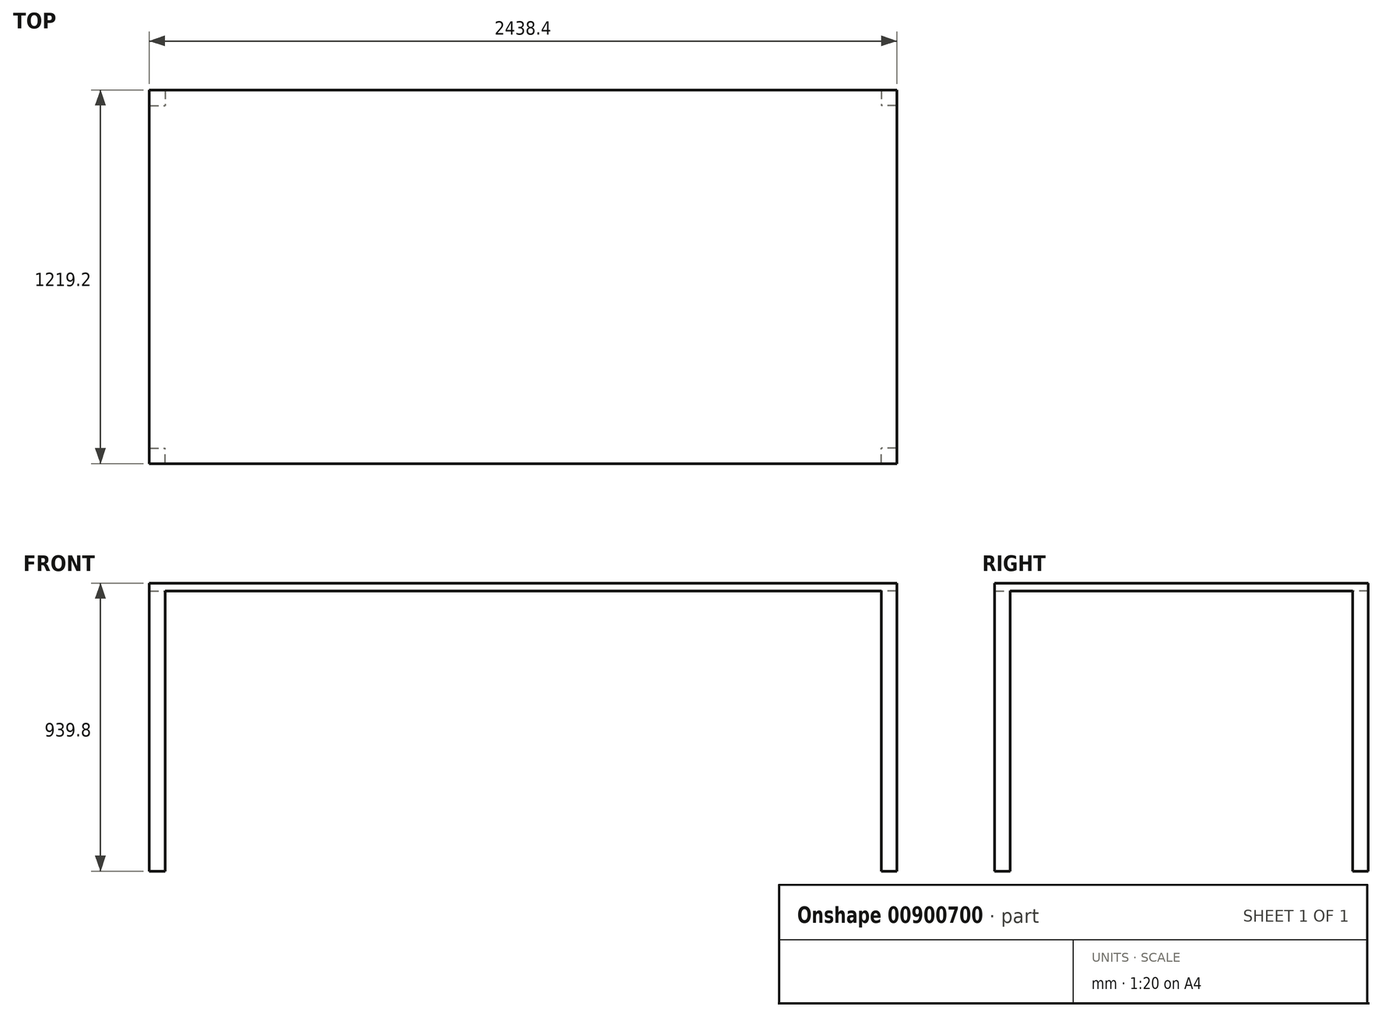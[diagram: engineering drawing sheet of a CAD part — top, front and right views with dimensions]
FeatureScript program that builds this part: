
annotation { "Feature Type Name" : "Feature", "Feature Type Description" : "" }
export const myFeature = defineFeature(function(context is Context, id is Id, definition is map)
    precondition{}
    {
        {
            var Q0;
            Q0=qCreatedBy(makeId("Top.planeOp"),FACE);
            var sketch = newSketch(context, id + "F0", { "sketchPlane" : qUnion([Q0])});
            skPoint(sketch, "E0.0", {"position": v(0, 0) * mm});
            skLineSegment(sketch, "E1.bottom", {"start": v(1.57, 0) * mm, "end": v(2439.97, 0) * mm});
            skLineSegment(sketch, "E1.top", {"start": v(1.57, 1219.2) * mm, "end": v(2439.97, 1219.2) * mm});
            skLineSegment(sketch, "E1.left", {"start": v(1.57, 0) * mm, "end": v(1.57, 1219.2) * mm});
            skLineSegment(sketch, "E1.right", {"start": v(2439.97, 0) * mm, "end": v(2439.97, 1219.2) * mm});
            skSolve(sketch);
        }
        {
            var Q0;
            Q0 = qSketchRegion(id + "F0", true);
            extrude(context, id + "F1", {"entities" : qUnion([Q0]), "depth" : 25.4 * mm, "offsetDistance" : 25.4 * mm});
        }
        {
            var Q0;
            Q0=makeQuery(id+"F1.opExtrude","CAP_FACE",FACE,{"disambiguationData":[OSD([sQuery(id+"F0.wireOp",EDGE,"E1.bottom"),sQuery(id+"F0.wireOp",EDGE,"E1.top"),sQuery(id+"F0.wireOp",EDGE,"E1.left"),sQuery(id+"F0.wireOp",EDGE,"E1.right")])],"isStart":true});
            var sketch = newSketch(context, id + "F2", { "sketchPlane" : qUnion([Q0])});
            skLineSegment(sketch, "E2.bottom", {"start": v(1.57, 0) * mm, "end": v(52.37, 0) * mm});
            skLineSegment(sketch, "E2.top", {"start": v(1.57, -50.8) * mm, "end": v(52.37, -50.8) * mm});
            skLineSegment(sketch, "E2.left", {"start": v(1.57, 0) * mm, "end": v(1.57, -50.8) * mm});
            skLineSegment(sketch, "E2.right", {"start": v(52.37, 0) * mm, "end": v(52.37, -50.8) * mm});
            skLineSegment(sketch, "E3.bottom", {"start": v(1.57, -1219.2) * mm, "end": v(52.37, -1219.2) * mm});
            skLineSegment(sketch, "E3.top", {"start": v(1.57, -1168.4) * mm, "end": v(52.37, -1168.4) * mm});
            skLineSegment(sketch, "E3.left", {"start": v(1.57, -1219.2) * mm, "end": v(1.57, -1168.4) * mm});
            skLineSegment(sketch, "E3.right", {"start": v(52.37, -1219.2) * mm, "end": v(52.37, -1168.4) * mm});
            skLineSegment(sketch, "E4.bottom", {"start": v(2439.97, 0) * mm, "end": v(2389.17, 0) * mm});
            skLineSegment(sketch, "E4.top", {"start": v(2439.97, -50.8) * mm, "end": v(2389.17, -50.8) * mm});
            skLineSegment(sketch, "E4.left", {"start": v(2439.97, 0) * mm, "end": v(2439.97, -50.8) * mm});
            skLineSegment(sketch, "E4.right", {"start": v(2389.17, 0) * mm, "end": v(2389.17, -50.8) * mm});
            skLineSegment(sketch, "E5.bottom", {"start": v(2439.97, -1219.2) * mm, "end": v(2389.17, -1219.2) * mm});
            skLineSegment(sketch, "E5.top", {"start": v(2439.97, -1168.4) * mm, "end": v(2389.17, -1168.4) * mm});
            skLineSegment(sketch, "E5.left", {"start": v(2439.97, -1219.2) * mm, "end": v(2439.97, -1168.4) * mm});
            skLineSegment(sketch, "E5.right", {"start": v(2389.17, -1219.2) * mm, "end": v(2389.17, -1168.4) * mm});
            skSolve(sketch);
        }
        {
            var Q0;
            Q0 = qSketchRegion(id + "F2", true);
            extrude(context, id + "F3", {"entities" : qUnion([Q0]), "operationType" : NewBodyOperationType.ADD, "depth" : 914.4 * mm, "offsetDistance" : 25.4 * mm});
        }
    });
